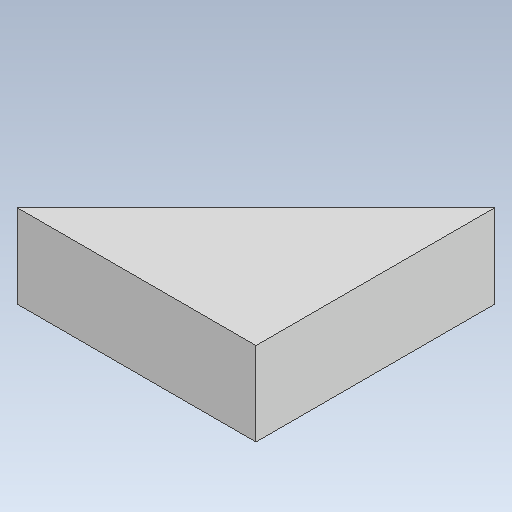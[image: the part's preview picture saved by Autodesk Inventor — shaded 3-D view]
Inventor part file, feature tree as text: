
AUTODESK INVENTOR PART (.ipt)
format: ipt  version: 2020 (Build 240168000, 168)  size: 90,112 bytes
history: native  units: mm
features: extrude x1, sketch x1
ambient origin geometry x8: Origin, YZ Plane, XZ Plane, XY Plane, X Axis, Y Axis, Z Axis, Center Point
bodies: Solid1 (feature_tree)
feature tree (2):
  extrude  "Extrusion1"  TaperAngle=90.0deg  [1 undecoded]
  sketch  "Sketch1"  dims[d2=7.0mm d3=0.0mm d6=90.0deg d7=45.0deg d8=20.0mm d9=20.0mm]
note: 1 required parameter value undecoded (feature->parameter linkage not recoverable at this tier; creation-order binding heuristic only, values carry confidence <= 0.55)
